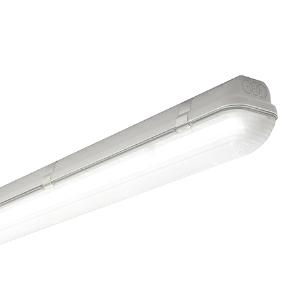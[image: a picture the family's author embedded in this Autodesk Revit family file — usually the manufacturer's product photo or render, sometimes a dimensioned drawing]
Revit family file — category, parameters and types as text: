
# Revit family: 3f_filippi_-_3f_linda_soft_3f_filippi_-_58733_-_3f_linda_led_soft_1x24w_l1270
name_source: partatom
category: Lighting Fixtures
units: mm (PartAtom-declared; Revit-internal decimal feet)

## family parameters
Cut with Voids When Loaded = No
Host = Face
Light Source = No
Part Type = Normal
Room Calculation Point = No
Round Connector Dimension = Use Diameter
Shared = No

## types (1)
- 3F Filippi - 3F Linda Soft (1 x LED, 3732 lm, 28 W, 4000 K)
    Apparent Load = 28 VA
    Approval mark = CE
    CIE Flux Codes = 39 68 88 89 100
    Color Rendering = 80
    Color Temperature = 4000 K
    Control Gear = Electronic ballast
    Default Elevation = 1800 mm
    Description = ILLUMINOTECHNICAL
Luminous efficiency 100% (DLOR 89%, ULOR 11%).
Initial luminous flux of the luminaire 3732 lm.
Direct symmetric distribution.
Installation Interdistance Transv.D = 1.39 x hu - Long.D = 1.21 x hu.
Tabular UGR (CIE 117 - 4H-8H; S=0.25H; 70/50/20): RUG 23.9 - 20.8.
Beam angle: 149° - 108°.
Luminous efficacy 133 lm/W.
Lifetime (L93/B10): 30000 h. (tq+25°C)
Lifetime (L90/B10): 50000 h. (tq+25°C)
Lifetime (L85/B10): 80000 h. (tq+25°C)
Lifetime (L80/B10): 100000 h. (tq+25°C)
Lifetime (L85/B10): 50000 h. (tq+35°C)
Sudden decreased luminous flux after 50000 hours: 0% (C0).
Photobiological safety in compliance with IEC/TR 62778: RG0 risk exempt, (IEC 62471).
In compliance with IEC/EN 62722-2-1 - IEC/EN 62717 standards.

SOURCE
Linear LED module 24W/840.
Energy efficiency class (UE 2019/2020 - UE 2019/2015): D.
CIE 13.3 Colour rendering index: CRI >80 (R9 <50%).
IES TM-30 Fidelity Index: Rf = 84 Rg = 95.
CCT nominal colour temperature 4000 K.
Colour initial tolerance (MacAdam): SDCM 3.

MECHANICAL
Self-extinguishing V2 polycarbonate housing, injection moulded, RAL 7035 grey.
Ecologic anti-aging injected sealing gasket.
Soft opal diffuser in self-extinguishing V2 polycarbonate, photo-engraved interior, UV stabilised, injection moulded.
Gear-holder reflector in hot-dip galvanised steel, painted with white polyester base.
Snug fit safety snap-lock clips for diffuser mounting in stainless steel, screwdriver opening.
Fixing brackets in stainless steel.
Possibility for technicians to access the interior of the luminaire.
Luminaire with limited surface temperature. - D - (EN 60598-2-24)
Dimensions: 1270x100 mm, height 100 mm. Weight 2.075 kg.
IP66 protection degree.
Mechanical strength to impacts IK10 (20 joule).
Glow-wire test resistance 850°C.

ELECTRICAL
Halogen Free electronic wiring 230V-50/60Hz, power factor 0.90, THD <25%, constant output current, SELV, class I, 1 driver.
Power of the luminaire 28 W.
ENEC - CE.
SAFE FLICKER: PstLM=<1 and SVM=<0.4 (IEC TR 61547-1 and IEC TR 63158), to ensure a more comfortable and safe light.
Luminaire compliant with EN 60598-2-22 for power supply from a centralised emergency system CPSS (Central Power Supply System), not incorporated in the luminaire - high risk areas excluded. The default power and flux are 100% in AC and 100% in DC.
Ambient temperature from -20°C to +35°C.
Temperature class T6 max 85°C.
Relative humidity UR: <85%.

INSTALLATION
Ceiling / Suspended / Wall.
All accessories dedicated to this product are available on the Catalog and on our website www.3F-Filippi.com.

APPLICATIONS
Suitable product for food production plants (HACCP), IFS (Food Version 6), BRC (GSFS Food Version 7).
Dry, dusty indoor environments, subject to occasional water splashes.
Luminaires designed for diffuse direct/indirect lighting suitable to provide optimum visual comfort.
Transit areas, stairwells.
Virtually shatterproof polycarbonate compatibly with the fumes / atmospheres that compromise the elasticity of plastic materials.
Suitable for illumination of public car parks and parking grounds referred to DIN 67528:2018-04.

WARNING
Fixture not suitable for cold stores with an ambient temperature <0°C and/or relative humidity >85%.
Luminaire designed for disposal/recycling at end-of-life.
Replaceable (LED only) light source by a professional. Replaceable control gear by a professional.
    Height = 100 mm  [stored 0.328084 ft]
    Lamp = 1 x LED
    Lamp Light Flux = 3732 lm
    Lamp Power = 28 W
    Lamp count = 1
    Length = 1270 mm
    Lifetime = 50000 h
    Luminous efficacy = 133 lm/W
    Manufacturer = 3F Filippi
    ModVariant = No
    Model = 3F Filippi - 58733 - 3F Linda LED Soft 1x24W L1270
    Mounting Place = Ceiling
    Mounting Type = Pendant
    Number of Poles = 1
    OnlyDefault = Yes
    Power Factor = 1
    Product Name = 3F Filippi - 3F Linda Soft
    Product group = pendant luminaire
    ProductGroupID = 9
    Protection Class = Protection class I
    Protection Degree = IP 66
    RLX_Detail_Level = 1
    RLX_Emergency_Light_Flux = 0 lm
    RLX_Emergency_Type = 0
    RLX_Emergency_Type_DB = No
    RlxData = <blob elided: 59381 chars, md5=4c741a8b>
    Socket = socket
    Standby Power = 0 W
    System Light Flux = 3732 lm
    System Power = 28 W
    Type Comments = Product without accessories
    Type Image = 3ffilippi_3f_linda_led_soft_1x.jpg
    URL = http://relux.com
    VarID = ---
    Voltage = 0 V
    Weight = 0.00 kg
    Width = 100 mm  [stored 0.328084 ft]

note: [stored X ft] marks values corroborated as IEEE doubles in the binary element streams (Revit-internal decimal feet)

## geometry (parser evidence)
native form markers: Blend x4, Sweep x12
no freeform markers — native parametric forms only
